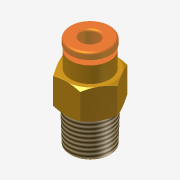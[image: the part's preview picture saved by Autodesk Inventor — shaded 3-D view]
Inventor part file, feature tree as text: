
AUTODESK INVENTOR PART (.ipt)
format: ipt  version: 2014 SP1 (Build 180222100, 222)  size: 165,888 bytes
history: native  units: in
note: dims shown in document units (in); Inventor stores cm internally (conversion verified against a paired STEP export)
features: imported_body x1, thread x1
ambient origin geometry x8: Origin, YZ Plane, XZ Plane, XY Plane, X Axis, Y Axis, Z Axis, Center Point
bodies: Solid1 (feature_tree)
feature tree (2):
  imported_body  "Base1"
  thread  "Thread1"  [1 undecoded]
note: 1 required parameter value undecoded (feature->parameter linkage not recoverable at this tier; creation-order binding heuristic only, values carry confidence <= 0.55)
